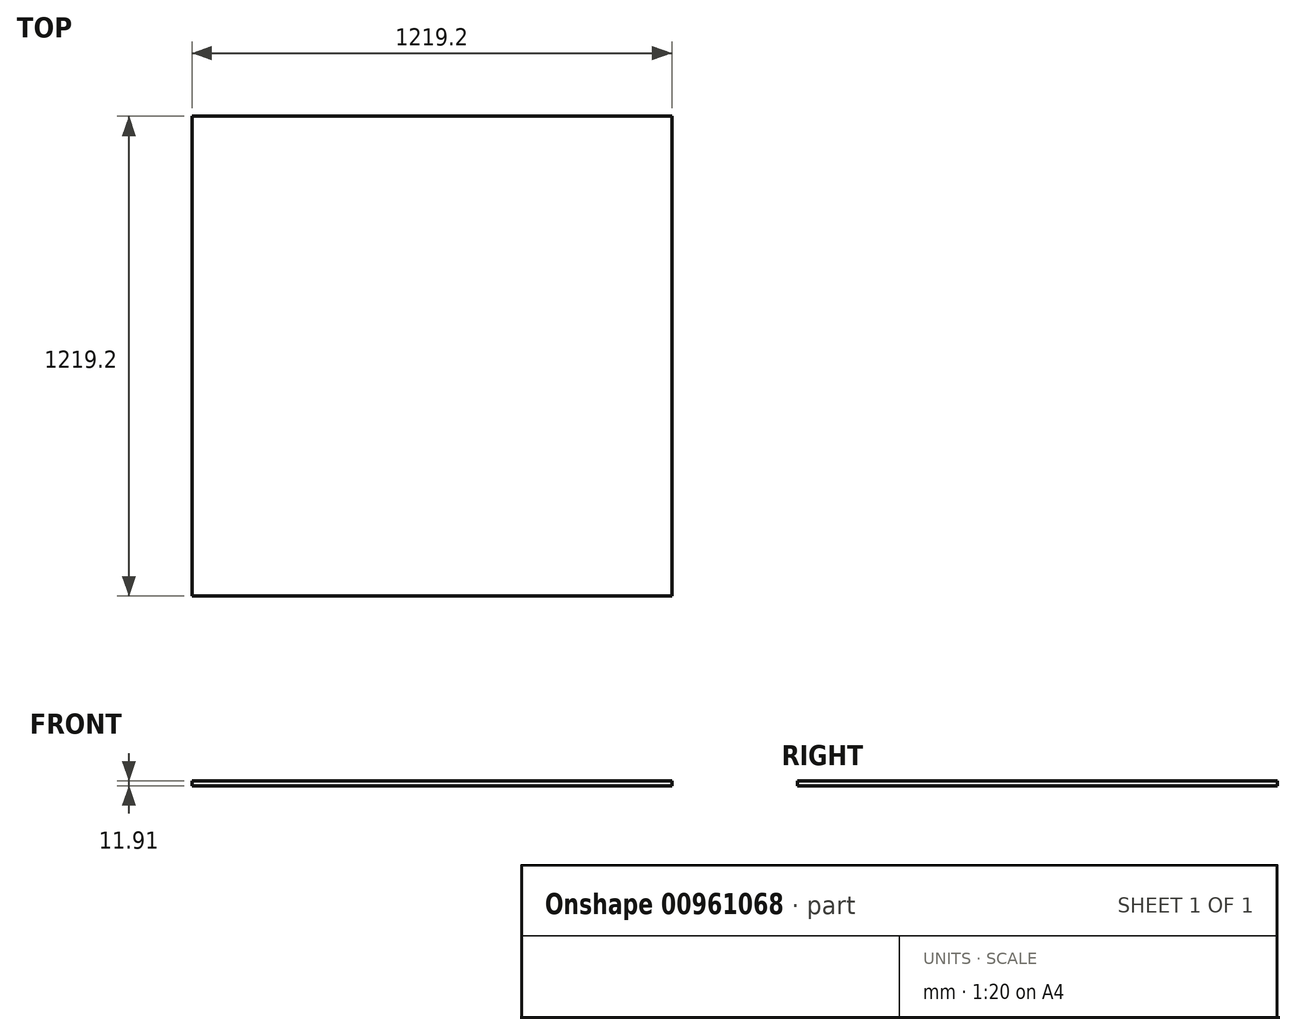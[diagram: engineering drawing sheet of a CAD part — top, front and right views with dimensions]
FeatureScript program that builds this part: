
annotation { "Feature Type Name" : "Feature", "Feature Type Description" : "" }
export const myFeature = defineFeature(function(context is Context, id is Id, definition is map)
    precondition{}
    {
        {
            var Q0;
            Q0=qCreatedBy(makeId("Front.planeOp"),FACE);
            var sketch = newSketch(context, id + "F0", { "sketchPlane" : qUnion([Q0])});
            skLineSegment(sketch, "E0.bottom", {"start": v(-366.63, 36.44) * mm, "end": v(852.57, 36.44) * mm});
            skLineSegment(sketch, "E0.top", {"start": v(-366.63, 48.35) * mm, "end": v(852.57, 48.35) * mm});
            skLineSegment(sketch, "E0.left", {"start": v(-366.63, 36.44) * mm, "end": v(-366.63, 48.35) * mm});
            skLineSegment(sketch, "E0.right", {"start": v(852.57, 36.44) * mm, "end": v(852.57, 48.35) * mm});
            skLineSegment(sketch, "E1.bottom", {"start": v(-1762, 47.6) * mm, "end": v(-542.8, 47.6) * mm});
            skLineSegment(sketch, "E1.top", {"start": v(-1762, 59.5) * mm, "end": v(-542.8, 59.5) * mm});
            skLineSegment(sketch, "E1.left", {"start": v(-1762, 47.6) * mm, "end": v(-1762, 59.5) * mm});
            skLineSegment(sketch, "E1.right", {"start": v(-542.8, 47.6) * mm, "end": v(-542.8, 59.5) * mm});
            skSolve(sketch);
        }
        {
            var Q0;
            Q0=makeQuery(id+"F0.imprint","IMPRINT",FACE,{"disambiguationData":[TD([[makeQuery(id+"F0.imprint","IMPRINT",EDGE,{"derivedFrom":sQuery(id+"F0.wireOp",EDGE,"E0.bottom")}),1.0]])]});
            extrude(context, id + "F1", {"entities" : qUnion([Q0]), "depth" : 1219.2 * mm, "offsetDistance" : 25.4 * mm});
        }
    });
